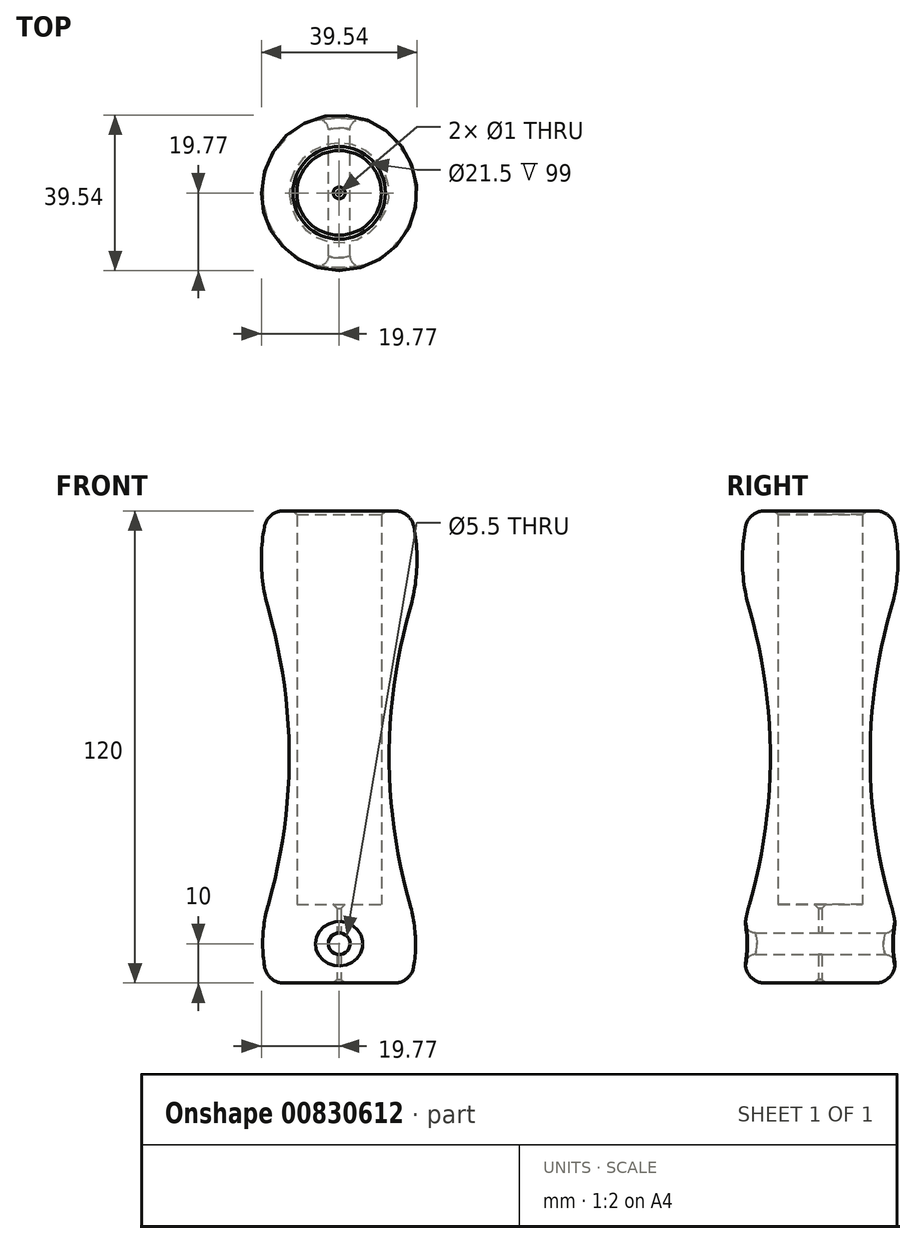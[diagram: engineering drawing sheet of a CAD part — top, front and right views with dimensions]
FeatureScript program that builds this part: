
annotation { "Feature Type Name" : "Feature", "Feature Type Description" : "" }
export const myFeature = defineFeature(function(context is Context, id is Id, definition is map)
    precondition{}
    {
        {
            var Q0;
            Q0=qCreatedBy(makeId("Front.planeOp"),FACE);
            var sketch = newSketch(context, id + "F0", { "sketchPlane" : qUnion([Q0])});
            skLineSegment(sketch, "E0", {"start": v(0, 0) * mm, "end": v(0, 124.26) * mm, "construction": true});
            skLineSegment(sketch, "E1", {"start": v(0.5, 0) * mm, "end": v(18, 0) * mm});
            skLineSegment(sketch, "E2", {"start": v(18, 0) * mm, "end": v(18, 120) * mm, "construction": true});
            skLineSegment(sketch, "E3", {"start": v(18, 120) * mm, "end": v(0, 120) * mm, "construction": true});
            skLineSegment(sketch, "E4", {"start": v(0, 95) * mm, "end": v(18, 95) * mm, "construction": true});
            skLineSegment(sketch, "E5", {"start": v(0, 20) * mm, "end": v(18, 20) * mm, "construction": true});
            skArc(sketch, "E6", {"start": v(18, 95) * mm, "mid": v(19.77, 107.5) * mm, "end": v(18, 120) * mm});
            skArc(sketch, "E7", {"start": v(18, 95) * mm, "mid": v(12.69, 57.5) * mm, "end": v(18, 20) * mm});
            skArc(sketch, "E8", {"start": v(18, 0) * mm, "mid": v(19.42, 10) * mm, "end": v(18, 20) * mm});
            skLineSegment(sketch, "E9", {"start": v(0.5, 20) * mm, "end": v(10.75, 20) * mm});
            skLineSegment(sketch, "E10", {"start": v(10.75, 20) * mm, "end": v(10.75, 120) * mm});
            skLineSegment(sketch, "E11", {"start": v(10.75, 120) * mm, "end": v(18, 120) * mm});
            skLineSegment(sketch, "E12", {"start": v(0.5, 20) * mm, "end": v(0.5, 0) * mm});
            skSolve(sketch);
        }
        {
            var Q0;
            Q0=makeQuery(id+"F0.imprint","IMPRINT",FACE,{"disambiguationData":[TD([[makeQuery(id+"F0.imprint","IMPRINT",EDGE,{"derivedFrom":sQuery(id+"F0.wireOp",EDGE,"E1")}),1.0]])]});
            var Q1;
            Q1=sQuery(id+"F0.wireOp",EDGE,"E0");
            revolve(context, id + "F1", {"surfaceOperationType" : NewSurfaceOperationType.NEW, "entities" : qUnion([Q0]), "axis" : qUnion([Q1]), "revolveType" : RevolveType.FULL});
        }
        {
            var Q0;
            Q0=makeQuery(id+"F1.opRevolve","SWEPT_EDGE",EDGE,{"disambiguationData":[OSD([sQuery(id+"F0.wireOp",EDGE,"E6"),sQuery(id+"F0.wireOp",EDGE,"E11")])]});
            var Q1;
            Q1=makeQuery(id+"F1.opRevolve","SWEPT_EDGE",EDGE,{"disambiguationData":[OSD([sQuery(id+"F0.wireOp",EDGE,"E1"),sQuery(id+"F0.wireOp",EDGE,"E8")])]});
            fillet(context, id + "F2", {"entities" : qUnion([Q0, Q1]), "radius" : 5 * mm, "tangentPropagation" : true, "allowEdgeOverflow" : false});
        }
        {
            var Q0;
            Q0=qCreatedBy(makeId("Front.planeOp"),FACE);
            var sketch = newSketch(context, id + "F3", { "sketchPlane" : qUnion([Q0])});
            skCircle(sketch, "E13", {"center": v(0, 10) * mm, "radius": 2.75 * mm});
            skSolve(sketch);
        }
        {
            var Q0;
            Q0=qSketchRegion(id+"F3",true);
            extrude(context, id + "F4", {"entities" : qUnion([Q0]), "operationType" : NewBodyOperationType.REMOVE, "endBound" : BoundingType.SYMMETRIC, "depth" : 40 * mm, "offsetDistance" : 25 * mm});
        }
        {
            var Q0;
            Q0=makeQuery(id+"F4.boolean.opBoolean","INTERSECT",EDGE,{"disambiguationData":[OD(0.0)],"derivedFrom":[makeQuery(id+"F1.opRevolve","SWEPT_FACE",FACE,{"disambiguationData":[OSD([sQuery(id+"F0.wireOp",EDGE,"E8")])]}),makeQuery(id+"F4.opExtrude","SWEPT_FACE",FACE,{"disambiguationData":[OSD([sQuery(id+"F3.wireOp",EDGE,"E13")])]})]});
            var Q1;
            Q1=makeQuery(id+"F4.boolean.opBoolean","INTERSECT",EDGE,{"disambiguationData":[OD(1.0)],"derivedFrom":[makeQuery(id+"F1.opRevolve","SWEPT_FACE",FACE,{"disambiguationData":[OSD([sQuery(id+"F0.wireOp",EDGE,"E8")])]}),makeQuery(id+"F4.opExtrude","SWEPT_FACE",FACE,{"disambiguationData":[OSD([sQuery(id+"F3.wireOp",EDGE,"E13")])]})]});
            fillet(context, id + "F5", {"entities" : qUnion([Q0, Q1]), "radius" : 2.5 * mm, "tangentPropagation" : true, "allowEdgeOverflow" : false});
        }
        {
            var Q0;
            Q0=makeQuery(id+"F1.opRevolve","SWEPT_EDGE",EDGE,{"disambiguationData":[OSD([sQuery(id+"F0.wireOp",EDGE,"E10"),sQuery(id+"F0.wireOp",EDGE,"E11")])]});
            var Q1;
            Q1=makeQuery(id+"F1.opRevolve","SWEPT_EDGE",EDGE,{"disambiguationData":[OSD([sQuery(id+"F0.wireOp",EDGE,"E1"),sQuery(id+"F0.wireOp",EDGE,"E12")])]});
            var Q2;
            Q2=makeQuery(id+"F1.opRevolve","SWEPT_EDGE",EDGE,{"disambiguationData":[OSD([sQuery(id+"F0.wireOp",EDGE,"E9"),sQuery(id+"F0.wireOp",EDGE,"E12")])]});
            chamfer(context, id + "F6", {"entities" : qUnion([Q0, Q1, Q2]), "width" : 1 * mm, "tangentPropagation" : true});
        }
    });
